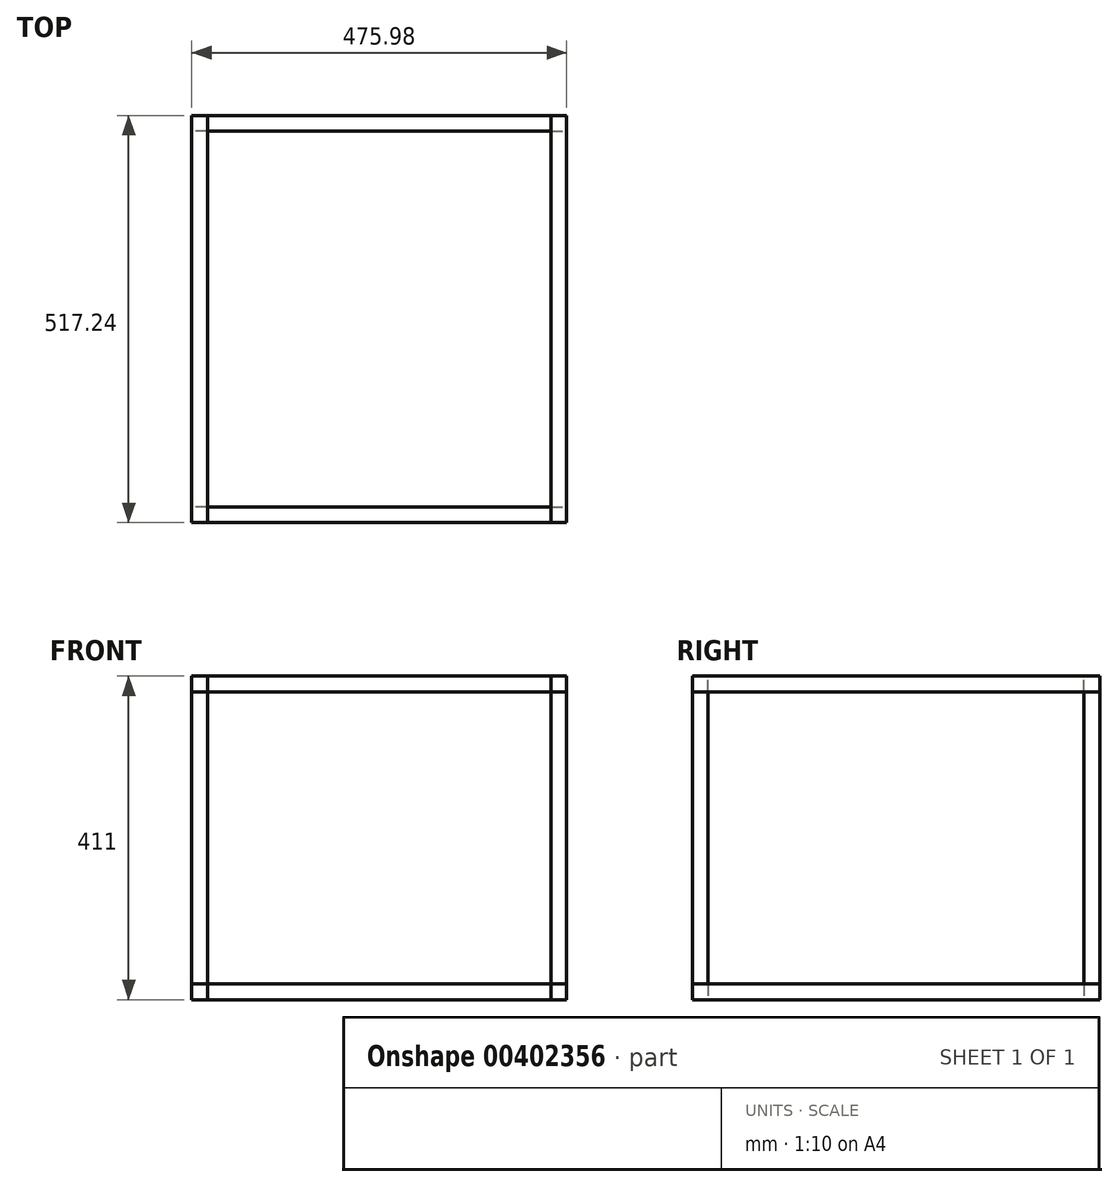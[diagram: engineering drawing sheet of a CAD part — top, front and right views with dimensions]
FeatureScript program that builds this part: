
annotation { "Feature Type Name" : "Feature", "Feature Type Description" : "" }
export const myFeature = defineFeature(function(context is Context, id is Id, definition is map)
    precondition{}
    {
        {
            var Q0;
            Q0=qCreatedBy(makeId("Top.planeOp"),FACE);
            var sketch = newSketch(context, id + "F0", { "sketchPlane" : qUnion([Q0])});
            skLineSegment(sketch, "E0.bottom", {"start": v(217.99, 238.63) * mm, "end": v(-217.99, 238.62) * mm, "construction": true});
            skLineSegment(sketch, "E0.top", {"start": v(217.99, -238.62) * mm, "end": v(-217.99, -238.63) * mm, "construction": true});
            skLineSegment(sketch, "E0.left", {"start": v(217.99, 238.63) * mm, "end": v(217.99, -238.62) * mm, "construction": true});
            skLineSegment(sketch, "E0.right", {"start": v(-217.99, 238.62) * mm, "end": v(-217.99, -238.62) * mm, "construction": true});
            skPoint(sketch, "E0.middle", {"position": v(0, 0) * mm});
            skLineSegment(sketch, "E1.bottom", {"start": v(217.99, 238.63) * mm, "end": v(237.99, 238.63) * mm});
            skLineSegment(sketch, "E1.top", {"start": v(217.99, 258.63) * mm, "end": v(237.99, 258.63) * mm});
            skLineSegment(sketch, "E1.left", {"start": v(217.99, 238.63) * mm, "end": v(217.99, 258.63) * mm});
            skLineSegment(sketch, "E1.right", {"start": v(237.99, 238.63) * mm, "end": v(237.99, 258.63) * mm});
            skLineSegment(sketch, "E2.bottom", {"start": v(217.99, -238.62) * mm, "end": v(237.99, -238.62) * mm});
            skLineSegment(sketch, "E2.top", {"start": v(217.99, -258.62) * mm, "end": v(237.99, -258.62) * mm});
            skLineSegment(sketch, "E2.left", {"start": v(217.99, -238.62) * mm, "end": v(217.99, -258.62) * mm});
            skLineSegment(sketch, "E2.right", {"start": v(237.99, -238.62) * mm, "end": v(237.99, -258.62) * mm});
            skLineSegment(sketch, "E3.bottom", {"start": v(-217.99, 238.62) * mm, "end": v(-237.99, 238.62) * mm});
            skLineSegment(sketch, "E3.top", {"start": v(-217.99, 258.62) * mm, "end": v(-237.99, 258.62) * mm});
            skLineSegment(sketch, "E3.left", {"start": v(-217.99, 238.62) * mm, "end": v(-217.99, 258.62) * mm});
            skLineSegment(sketch, "E3.right", {"start": v(-237.99, 238.62) * mm, "end": v(-237.99, 258.62) * mm});
            skLineSegment(sketch, "E4.bottom", {"start": v(-217.99, -238.62) * mm, "end": v(-237.99, -238.62) * mm});
            skLineSegment(sketch, "E4.top", {"start": v(-217.99, -258.62) * mm, "end": v(-237.99, -258.62) * mm});
            skLineSegment(sketch, "E4.left", {"start": v(-217.99, -238.62) * mm, "end": v(-217.99, -258.62) * mm});
            skLineSegment(sketch, "E4.right", {"start": v(-237.99, -238.62) * mm, "end": v(-237.99, -258.62) * mm});
            skSolve(sketch);
        }
        {
            var Q0;
            Q0=makeQuery(id+"F0.imprint","IMPRINT",FACE,{"disambiguationData":[TD([[makeQuery(id+"F0.imprint","IMPRINT",EDGE,{"derivedFrom":sQuery(id+"F0.wireOp",EDGE,"E1.bottom")}),1.0]])]});
            var Q1;
            Q1=makeQuery(id+"F0.imprint","IMPRINT",FACE,{"disambiguationData":[TD([[makeQuery(id+"F0.imprint","IMPRINT",EDGE,{"derivedFrom":sQuery(id+"F0.wireOp",EDGE,"E3.bottom")}),-1.0]])]});
            var Q2;
            Q2=makeQuery(id+"F0.imprint","IMPRINT",FACE,{"disambiguationData":[TD([[makeQuery(id+"F0.imprint","IMPRINT",EDGE,{"derivedFrom":sQuery(id+"F0.wireOp",EDGE,"E4.bottom")}),1.0]])]});
            var Q3;
            Q3=makeQuery(id+"F0.imprint","IMPRINT",FACE,{"disambiguationData":[TD([[makeQuery(id+"F0.imprint","IMPRINT",EDGE,{"derivedFrom":sQuery(id+"F0.wireOp",EDGE,"E2.bottom")}),-1.0]])]});
            extrude(context, id + "F1", {"entities" : qUnion([Q0, Q1, Q2, Q3]), "depth" : 371 * mm});
        }
        {
            var Q0;
            Q0=makeQuery(id+"F1.opExtrude","SWEPT_FACE",FACE,{"disambiguationData":[OSD([sQuery(id+"F0.wireOp",EDGE,"E1.left")])]});
            var sketch = newSketch(context, id + "F2", { "sketchPlane" : qUnion([Q0])});
            skLineSegment(sketch, "E5.bottom", {"start": v(-258.62, 371) * mm, "end": v(-238.62, 371) * mm});
            skLineSegment(sketch, "E5.top", {"start": v(-258.62, 391) * mm, "end": v(-238.62, 391) * mm});
            skLineSegment(sketch, "E5.left", {"start": v(-258.62, 371) * mm, "end": v(-258.62, 391) * mm});
            skLineSegment(sketch, "E5.right", {"start": v(-238.62, 371) * mm, "end": v(-238.62, 391) * mm});
            skLineSegment(sketch, "E6.bottom", {"start": v(238.62, 371) * mm, "end": v(258.62, 371) * mm});
            skLineSegment(sketch, "E6.top", {"start": v(238.62, 391) * mm, "end": v(258.62, 391) * mm});
            skLineSegment(sketch, "E6.left", {"start": v(238.62, 371) * mm, "end": v(238.62, 391) * mm});
            skLineSegment(sketch, "E6.right", {"start": v(258.62, 371) * mm, "end": v(258.62, 391) * mm});
            skLineSegment(sketch, "E7.bottom", {"start": v(-258.62, 0) * mm, "end": v(-238.62, 0) * mm});
            skLineSegment(sketch, "E7.top", {"start": v(-258.62, -20) * mm, "end": v(-238.62, -20) * mm});
            skLineSegment(sketch, "E7.left", {"start": v(-258.62, 0) * mm, "end": v(-258.62, -20) * mm});
            skLineSegment(sketch, "E7.right", {"start": v(-238.62, 0) * mm, "end": v(-238.62, -20) * mm});
            skLineSegment(sketch, "E8.bottom", {"start": v(238.62, 0) * mm, "end": v(258.62, 0) * mm});
            skLineSegment(sketch, "E8.top", {"start": v(238.62, -20) * mm, "end": v(258.62, -20) * mm});
            skLineSegment(sketch, "E8.left", {"start": v(238.62, 0) * mm, "end": v(238.62, -20) * mm});
            skLineSegment(sketch, "E8.right", {"start": v(258.62, 0) * mm, "end": v(258.62, -20) * mm});
            skSolve(sketch);
        }
        {
            var Q0;
            Q0=makeQuery(id+"F2.imprint","IMPRINT",FACE,{"disambiguationData":[TD([[makeQuery(id+"F2.imprint","IMPRINT",EDGE,{"derivedFrom":sQuery(id+"F2.wireOp",EDGE,"E5.bottom")}),-1.0]])]});
            var Q1;
            Q1=makeQuery(id+"F2.imprint","IMPRINT",FACE,{"disambiguationData":[TD([[makeQuery(id+"F2.imprint","IMPRINT",EDGE,{"derivedFrom":sQuery(id+"F2.wireOp",EDGE,"E6.bottom")}),1.0]])]});
            var Q2;
            Q2=makeQuery(id+"F2.imprint","IMPRINT",FACE,{"disambiguationData":[TD([[makeQuery(id+"F2.imprint","IMPRINT",EDGE,{"derivedFrom":sQuery(id+"F2.wireOp",EDGE,"E7.bottom")}),1.0]])]});
            var Q3;
            Q3=makeQuery(id+"F2.imprint","IMPRINT",FACE,{"disambiguationData":[TD([[makeQuery(id+"F2.imprint","IMPRINT",EDGE,{"derivedFrom":sQuery(id+"F2.wireOp",EDGE,"E8.bottom")}),-1.0]])]});
            var Q4;
            Q4=makeQuery(id+"F1.opExtrude","SWEPT_FACE",FACE,{"disambiguationData":[OSD([sQuery(id+"F0.wireOp",EDGE,"E3.left")])]});
            extrude(context, id + "F3", {"entities" : qUnion([Q0, Q1, Q2, Q3]), "endBound" : BoundingType.UP_TO_SURFACE, "endBoundEntityFace" : qUnion([Q4]), "depth" : 25 * mm});
        }
        {
            var Q0;
            Q0=makeQuery(id+"F1.opExtrude","SWEPT_FACE",FACE,{"disambiguationData":[OSD([sQuery(id+"F0.wireOp",EDGE,"E1.top")])]});
            var sketch = newSketch(context, id + "F4", { "sketchPlane" : qUnion([Q0])});
            skLineSegment(sketch, "E9.bottom", {"start": v(-237.99, 391) * mm, "end": v(-217.99, 391) * mm});
            skLineSegment(sketch, "E9.top", {"start": v(-237.99, 371) * mm, "end": v(-217.99, 371) * mm});
            skLineSegment(sketch, "E9.left", {"start": v(-237.99, 391) * mm, "end": v(-237.99, 371) * mm});
            skLineSegment(sketch, "E9.right", {"start": v(-217.99, 391) * mm, "end": v(-217.99, 371) * mm});
            skPoint(sketch, "E10.firstSnap0", {"position": v(-227.99, 371) * mm});
            skPoint(sketch, "E10.oppositeSnap0", {"position": v(-227.99, 391) * mm});
            skLineSegment(sketch, "E10.bottom", {"start": v(217.99, 371) * mm, "end": v(237.99, 371) * mm});
            skLineSegment(sketch, "E10.top", {"start": v(217.99, 391) * mm, "end": v(237.99, 391) * mm});
            skLineSegment(sketch, "E10.left", {"start": v(217.99, 371) * mm, "end": v(217.99, 391) * mm});
            skLineSegment(sketch, "E10.right", {"start": v(237.99, 371) * mm, "end": v(237.99, 391) * mm});
            skLineSegment(sketch, "E11.bottom", {"start": v(217.99, 0) * mm, "end": v(237.99, 0) * mm});
            skLineSegment(sketch, "E11.top", {"start": v(217.99, -20) * mm, "end": v(237.99, -20) * mm});
            skLineSegment(sketch, "E11.left", {"start": v(217.99, 0) * mm, "end": v(217.99, -20) * mm});
            skLineSegment(sketch, "E11.right", {"start": v(237.99, 0) * mm, "end": v(237.99, -20) * mm});
            skLineSegment(sketch, "E12.bottom", {"start": v(-217.99, 0) * mm, "end": v(-237.99, 0) * mm});
            skLineSegment(sketch, "E12.top", {"start": v(-217.99, -20) * mm, "end": v(-237.99, -20) * mm});
            skLineSegment(sketch, "E12.left", {"start": v(-217.99, 0) * mm, "end": v(-217.99, -20) * mm});
            skLineSegment(sketch, "E12.right", {"start": v(-237.99, 0) * mm, "end": v(-237.99, -20) * mm});
            skSolve(sketch);
        }
        {
            var Q0;
            Q0=makeQuery(id+"F4.imprint","IMPRINT",FACE,{"disambiguationData":[TD([[makeQuery(id+"F4.imprint","IMPRINT",EDGE,{"derivedFrom":sQuery(id+"F4.wireOp",EDGE,"E12.bottom")}),1.0]])]});
            var Q1;
            Q1=makeQuery(id+"F4.imprint","IMPRINT",FACE,{"disambiguationData":[TD([[makeQuery(id+"F4.imprint","IMPRINT",EDGE,{"derivedFrom":sQuery(id+"F4.wireOp",EDGE,"E11.bottom")}),-1.0]])]});
            var Q2;
            Q2=makeQuery(id+"F4.imprint","IMPRINT",FACE,{"disambiguationData":[TD([[makeQuery(id+"F4.imprint","IMPRINT",EDGE,{"derivedFrom":sQuery(id+"F4.wireOp",EDGE,"E10.bottom")}),1.0]])]});
            var Q3;
            Q3=makeQuery(id+"F4.imprint","IMPRINT",FACE,{"disambiguationData":[TD([[makeQuery(id+"F4.imprint","IMPRINT",EDGE,{"derivedFrom":sQuery(id+"F4.wireOp",EDGE,"E9.bottom")}),-1.0]])]});
            var Q4;
            Q4=makeQuery(id+"F1.opExtrude","SWEPT_FACE",FACE,{"disambiguationData":[OSD([sQuery(id+"F0.wireOp",EDGE,"E2.top")])]});
            extrude(context, id + "F5", {"entities" : qUnion([Q0, Q1, Q2, Q3]), "endBound" : BoundingType.UP_TO_SURFACE, "oppositeDirection" : true, "endBoundEntityFace" : qUnion([Q4]), "depth" : 25 * mm});
        }
    });
